# Revit family: Sanitary_Shower-screens_Duscholux_DuschoGredel_DuschoBasic_Separator-Fixed-panel-shower-bath
name_source: partatom
category: Plumbing Fixtures
revit_build: Autodesk Revit 2017 (Build: 20160225_1515(x64)
units: mm (PartAtom-declared; Revit-internal decimal feet)

## family parameters
Always vertical = Yes
Cut with Voids When Loaded = No
OmniClass Number = 23.45.00.00
OmniClass Title = Sanitary, Laundry, and Cleaning Equipment
Part Type = Normal
Room Calculation Point = No
Round Connector Dimension = Use Diameter
Shared = No
Work Plane-Based = No

## types (3) — shared parameters
Assembly Code = C1030200
Brand = Duscholux
Certified Quality UNE EN 14428 = http://www.duscholux.es
Components = Eropean components
Configuration enclosure = http://configuratumampara.duscholux.es
Description = Fixed separator (Bath/Shower)
Design country = Spain / Germany
Edition number = 1
Environmental Management ISO 14001 = ECOEMBES Certificate
Fact Sheet = http://blob.duscholux.es
Glass Material = Glass_Material-Duscholux
Glass in Building UNE EN 12150 = CE Conformity marking
Height = 2000 mm  [stored 6.56168 ft]
IFC Classification = Furnishing Element
Image = http://www.duscholux.es
Lenght Support = 1000 mm  [stored 3.28084 ft]
Logo visivility = Yes
Maintenance and Cleaning = http://www.duscholux.es
Manufacturer = Duscholux Ibérica, S.A.
Manufacturer country = Spain
Manufacturer name = Duscholux Ibérica, S.A.
Max Height = 2000 mm  [stored 6.56168 ft]
Model = DuschoBasic
NBS Reference Code = 45-35-70
NBS Reference Description = Shower Enclosures
Net Weight (Kg) = 50
Offset Support = 50 mm  [stored 0.164042 ft]
Opening System = Fixed panel
Opening System Image = http://blob.duscholux.es
Optional = Towel rail / Shelf
Product family = Duscho Gredel
Product group = Fixed panel for shower or bath
Products = http://www.duscholux.es
Ref. = 6BI / 6BD
Series = Duscho Gredel
Technical Inspection Certificate (Applus) = http://www.duscholux.es
Text logo visibility = Yes
Thickness Safety Glass = 8 mm  [stored 0.0262467 ft]
UNSPSC Code = 30181507
URL = http://www.duscholux.es
Uniclass 2015 Code = PR-40-20-06-79
Uniclass 2015 Description = Shower Enclosures

## per-type parameters (varying)
| type | Frame Material | Min/Max Width | Width |
| Platinum Aluminium Finish | Platinum Aluminium Finish | 800 mm  [stored 2.62467 ft] | 800 mm  [stored 2.62467 ft] |
| Siver Matt Aluminium Finish | Silver Matt Aluminium Finish | 1200 mm | 1200 mm |
| White Aluminium Finish | White Aluminium Finish | 1200 mm | 1200 mm |

note: [stored X ft] marks values corroborated as IEEE doubles in the binary element streams (Revit-internal decimal feet)

## geometry (parser evidence)
native form markers: Sweep x3
no freeform markers — native parametric forms only
